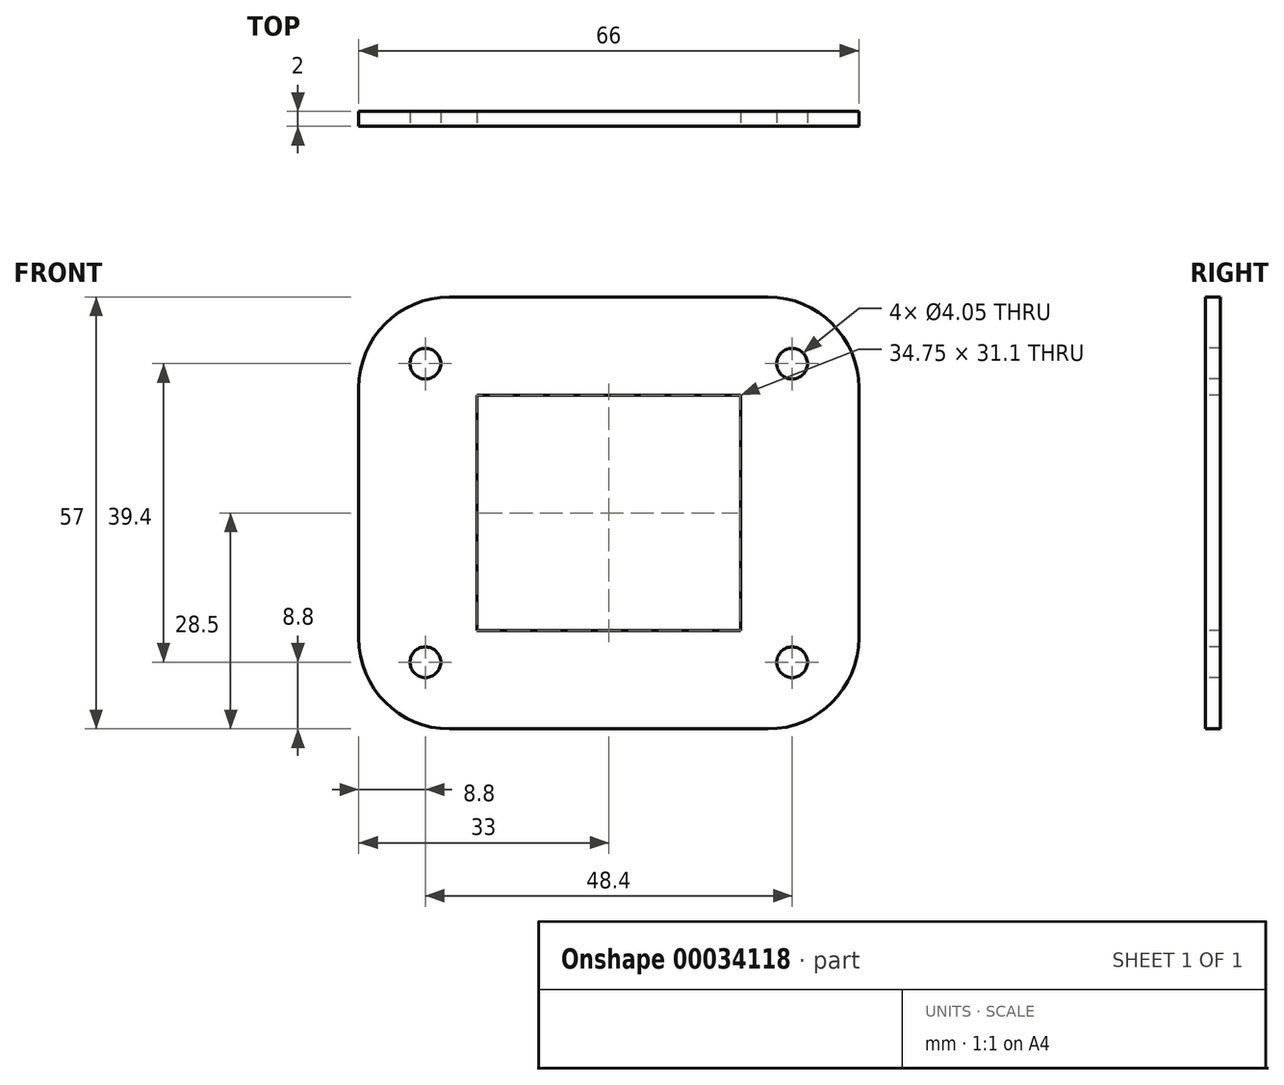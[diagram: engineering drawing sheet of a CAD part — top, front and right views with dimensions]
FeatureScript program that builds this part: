
annotation { "Feature Type Name" : "Feature", "Feature Type Description" : "" }
export const myFeature = defineFeature(function(context is Context, id is Id, definition is map)
    precondition{}
    {
        {
            var Q0;
            Q0=qCreatedBy(makeId("Front.planeOp"),FACE);
            var sketch = newSketch(context, id + "F0", { "sketchPlane" : qUnion([Q0])});
            skLineSegment(sketch, "E0.rect.bottom", {"start": v(21, -28.5) * mm, "end": v(-21, -28.5) * mm});
            skLineSegment(sketch, "E0.rect.top", {"start": v(21, 28.5) * mm, "end": v(-21, 28.5) * mm});
            skLineSegment(sketch, "E0.rect.left", {"start": v(33, -16.5) * mm, "end": v(33, 16.5) * mm});
            skLineSegment(sketch, "E0.rect.right", {"start": v(-33, -16.5) * mm, "end": v(-33, 16.5) * mm});
            skPoint(sketch, "E0.rect.middle", {"position": v(0, 0) * mm});
            skCircle(sketch, "E1", {"center": v(-24.2, 19.7) * mm, "radius": 2.02 * mm});
            skCircle(sketch, "E2", {"center": v(24.2, 19.7) * mm, "radius": 2.02 * mm});
            skCircle(sketch, "E3", {"center": v(24.2, -19.7) * mm, "radius": 2.02 * mm});
            skCircle(sketch, "E4", {"center": v(-24.2, -19.7) * mm, "radius": 2.02 * mm});
            skPoint(sketch, "E5.visualSharp", {"position": v(-33, 28.5) * mm});
            skArc(sketch, "E5.filletArc", {"start": v(-21, 28.5) * mm, "mid": v(-29.49, 24.99) * mm, "end": v(-33, 16.5) * mm});
            skPoint(sketch, "E6.visualSharp", {"position": v(-33, -28.5) * mm});
            skArc(sketch, "E6.filletArc", {"start": v(-33, -16.5) * mm, "mid": v(-29.49, -24.99) * mm, "end": v(-21, -28.5) * mm});
            skPoint(sketch, "E7.visualSharp", {"position": v(33, -28.5) * mm});
            skArc(sketch, "E7.filletArc", {"start": v(21, -28.5) * mm, "mid": v(29.49, -24.99) * mm, "end": v(33, -16.5) * mm});
            skPoint(sketch, "E8.visualSharp", {"position": v(33, 28.5) * mm});
            skArc(sketch, "E8.filletArc", {"start": v(33, 16.5) * mm, "mid": v(29.49, 24.99) * mm, "end": v(21, 28.5) * mm});
            skLineSegment(sketch, "E9.rect.bottom", {"start": v(17.38, -15.55) * mm, "end": v(-17.38, -15.55) * mm});
            skLineSegment(sketch, "E9.rect.top", {"start": v(17.38, 15.55) * mm, "end": v(-17.38, 15.55) * mm});
            skLineSegment(sketch, "E9.rect.left", {"start": v(17.38, -15.55) * mm, "end": v(17.38, 15.55) * mm});
            skLineSegment(sketch, "E9.rect.right", {"start": v(-17.38, -15.55) * mm, "end": v(-17.38, 15.55) * mm});
            skSolve(sketch);
        }
        {
            var Q0;
            Q0=makeQuery(id+"F0.imprint","IMPRINT",FACE,{"disambiguationData":[TD([[makeQuery(id+"F0.imprint","IMPRINT",EDGE,{"derivedFrom":sQuery(id+"F0.wireOp",EDGE,"E0.rect.bottom")}),-1.0]])]});
            extrude(context, id + "F1", {"entities" : qUnion([Q0]), "oppositeDirection" : true, "depth" : 2 * mm});
        }
    });
